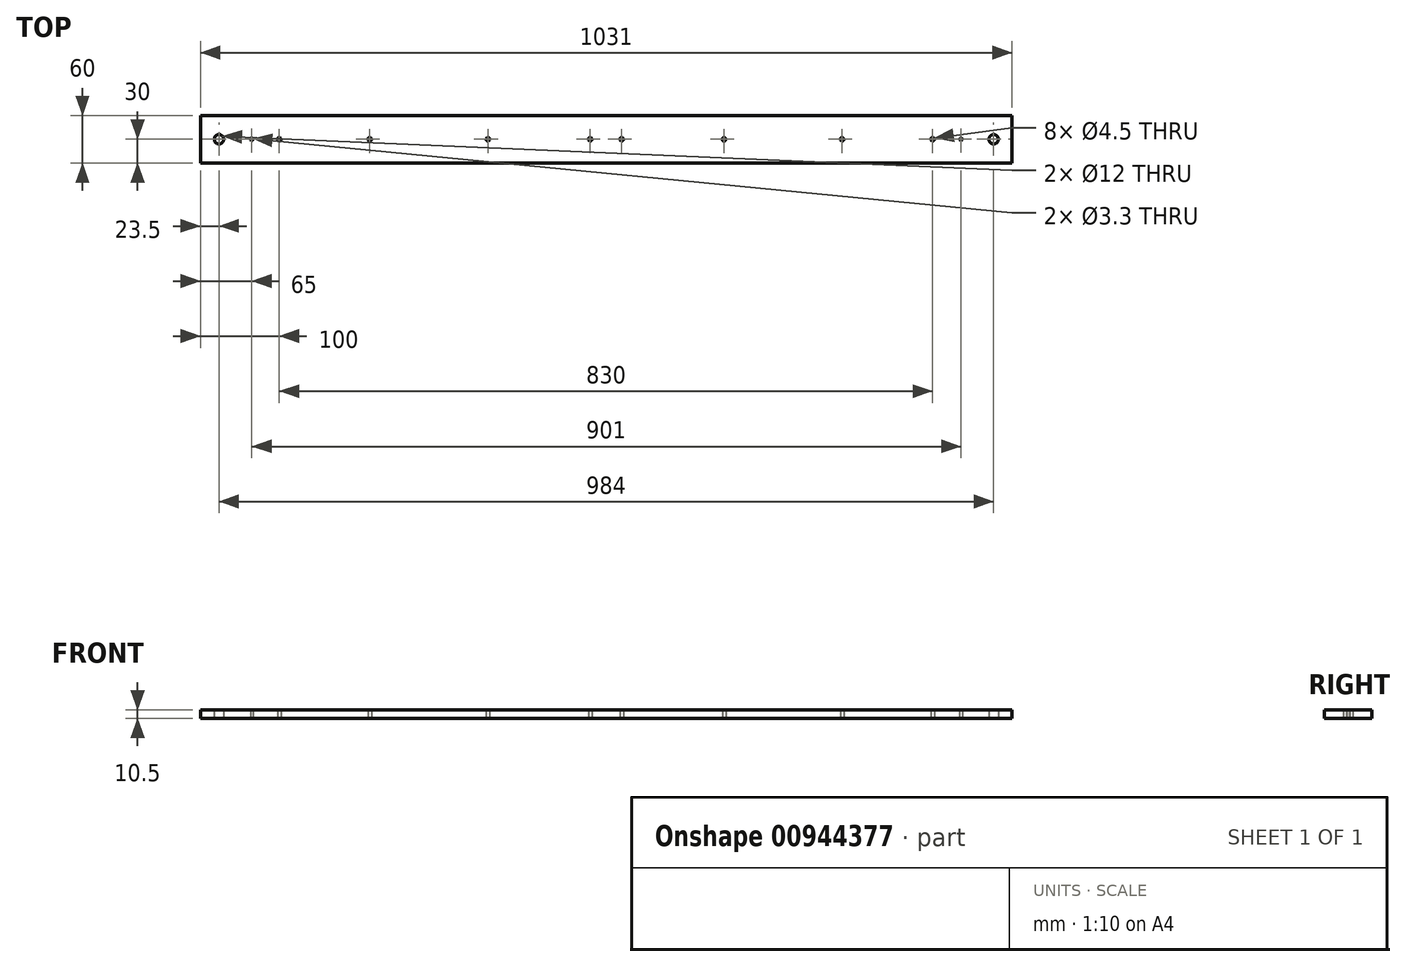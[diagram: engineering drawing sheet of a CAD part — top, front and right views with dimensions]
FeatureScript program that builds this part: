
annotation { "Feature Type Name" : "Feature", "Feature Type Description" : "" }
export const myFeature = defineFeature(function(context is Context, id is Id, definition is map)
    precondition{}
    {
        {
            var Q0;
            Q0=qCreatedBy(makeId("Top.planeOp"),FACE);
            var sketch = newSketch(context, id + "F0", { "sketchPlane" : qUnion([Q0])});
            skLineSegment(sketch, "E0.bottom", {"start": v(-515.5, 30) * mm, "end": v(515.5, 30) * mm});
            skLineSegment(sketch, "E0.top", {"start": v(-515.5, -30) * mm, "end": v(515.5, -30) * mm});
            skLineSegment(sketch, "E0.left", {"start": v(-515.5, 30) * mm, "end": v(-515.5, -30) * mm});
            skLineSegment(sketch, "E0.right", {"start": v(515.5, 30) * mm, "end": v(515.5, -30) * mm});
            skPoint(sketch, "E0.middle", {"position": v(0, 0) * mm});
            skLineSegment(sketch, "E1", {"start": v(-519.29, 0) * mm, "end": v(537.98, 0) * mm, "construction": true});
            skCircle(sketch, "E2", {"center": v(-492, 0) * mm, "radius": 6 * mm});
            skCircle(sketch, "E3", {"center": v(-450.5, 0) * mm, "radius": 1.65 * mm});
            skCircle(sketch, "E4", {"center": v(-415.5, 0) * mm, "radius": 2.25 * mm});
            skCircle(sketch, "E5", {"center": v(-300.5, 0) * mm, "radius": 2.25 * mm});
            skCircle(sketch, "E6", {"center": v(-150.5, 0) * mm, "radius": 2.25 * mm});
            skCircle(sketch, "E7", {"center": v(-20.5, 0) * mm, "radius": 2.25 * mm});
            skCircle(sketch, "E8", {"center": v(19.5, 0) * mm, "radius": 2.25 * mm});
            skLineSegment(sketch, "E9", {"start": v(0, 46.94) * mm, "end": v(0, -48.59) * mm, "construction": true});
            skPoint(sketch, "E9.startSnap0", {"position": v(0, 30) * mm});
            skPoint(sketch, "E9.endSnap0", {"position": v(0, -30) * mm});
            skCircle(sketch, "E10", {"center": v(149.5, 0) * mm, "radius": 2.25 * mm});
            skCircle(sketch, "E11", {"center": v(299.5, 0) * mm, "radius": 2.25 * mm});
            skCircle(sketch, "E12", {"center": v(414.5, 0) * mm, "radius": 2.25 * mm});
            skCircle(sketch, "E13", {"center": v(450.5, 0) * mm, "radius": 1.65 * mm});
            skCircle(sketch, "E14", {"center": v(492, 0) * mm, "radius": 6 * mm});
            skSolve(sketch);
        }
        {
            var Q0;
            Q0=makeQuery(id+"F0.imprint","IMPRINT",FACE,{"disambiguationData":[TD([[makeQuery(id+"F0.imprint","IMPRINT",EDGE,{"derivedFrom":sQuery(id+"F0.wireOp",EDGE,"E0.bottom")}),-1.0]])]});
            extrude(context, id + "F1", {"entities" : qUnion([Q0]), "depth" : 10.5 * mm, "offsetDistance" : 25 * mm});
        }
    });
